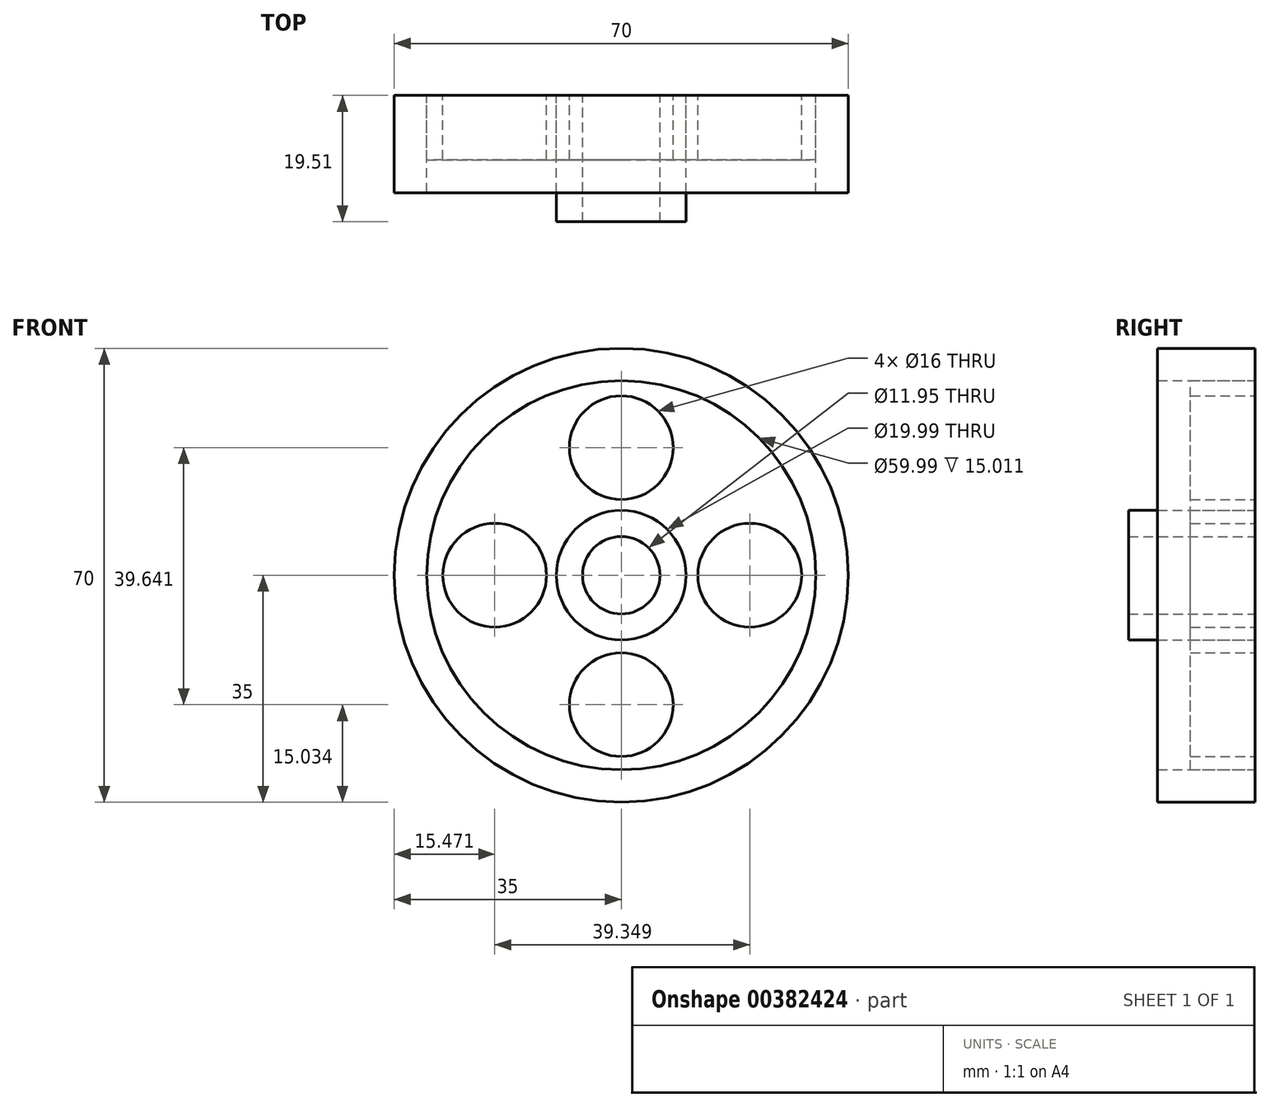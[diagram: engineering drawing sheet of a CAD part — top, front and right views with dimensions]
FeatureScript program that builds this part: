
annotation { "Feature Type Name" : "Feature", "Feature Type Description" : "" }
export const myFeature = defineFeature(function(context is Context, id is Id, definition is map)
    precondition{}
    {
        {
            var Q0;
            Q0=qCreatedBy(makeId("Front.planeOp"),FACE);
            var sketch = newSketch(context, id + "F0", { "sketchPlane" : qUnion([Q0])});
            skCircle(sketch, "E0", {"center": v(0, 0) * mm, "radius": 35 * mm});
            skCircle(sketch, "E1", {"center": v(0, 0) * mm, "radius": 30 * mm});
            skCircle(sketch, "E2", {"center": v(0, 0) * mm, "radius": 10 * mm});
            skCircle(sketch, "E3", {"center": v(0, 0) * mm, "radius": 5.98 * mm});
            skCircle(sketch, "E4", {"center": v(0, 19.67) * mm, "radius": 8 * mm});
            skCircle(sketch, "E5", {"center": v(19.82, 0) * mm, "radius": 8 * mm});
            skCircle(sketch, "E6", {"center": v(0, -19.97) * mm, "radius": 8 * mm});
            skCircle(sketch, "E7", {"center": v(-19.53, 0) * mm, "radius": 8 * mm});
            skSolve(sketch);
        }
        {
            var Q0;
            Q0=makeQuery(id+"F0.imprint","IMPRINT",FACE,{"disambiguationData":[TD([[makeQuery(id+"F0.imprint","IMPRINT",EDGE,{"derivedFrom":sQuery(id+"F0.wireOp",EDGE,"E0")}),1.0]])]});
            extrude(context, id + "F1", {"entities" : qUnion([Q0]), "depth" : 15 * mm});
        }
        {
            var Q0;
            Q0=makeQuery(id+"F0.imprint","IMPRINT",FACE,{"disambiguationData":[TD([[makeQuery(id+"F0.imprint","IMPRINT",EDGE,{"derivedFrom":sQuery(id+"F0.wireOp",EDGE,"E2")}),1.0]])]});
            extrude(context, id + "F2", {"entities" : qUnion([Q0]), "depth" : 19.5 * mm});
        }
        {
            var Q0;
            Q0=makeQuery(id+"F0.imprint","IMPRINT",FACE,{"disambiguationData":[TD([[makeQuery(id+"F0.imprint","IMPRINT",EDGE,{"derivedFrom":sQuery(id+"F0.wireOp",EDGE,"E1")}),1.0]])]});
            extrude(context, id + "F3", {"entities" : qUnion([Q0]), "depth" : 9.93 * mm});
        }
    });
